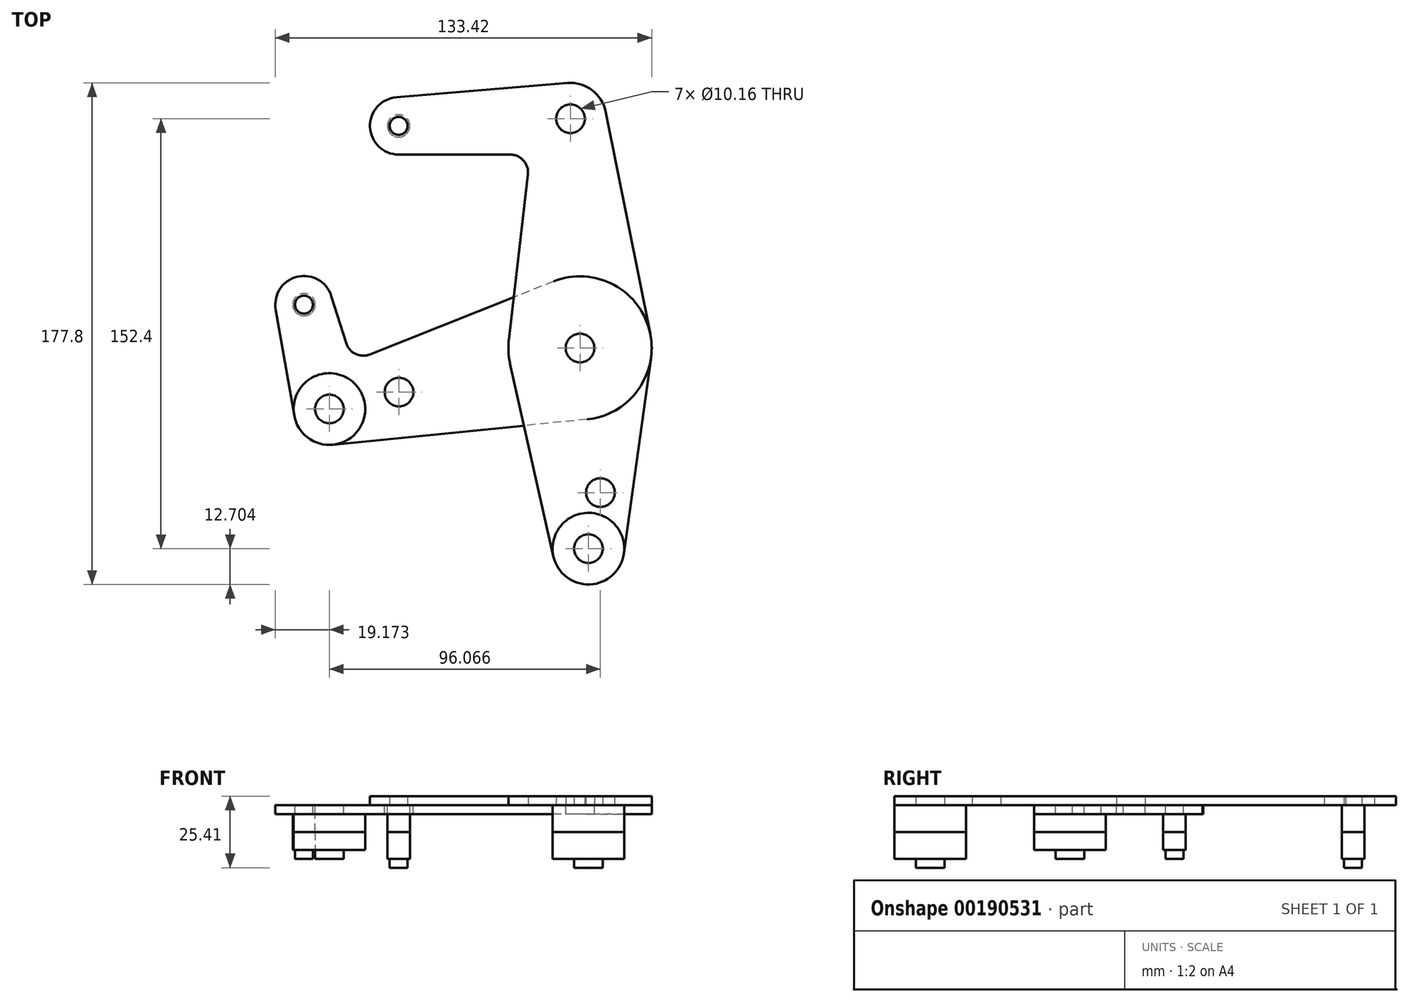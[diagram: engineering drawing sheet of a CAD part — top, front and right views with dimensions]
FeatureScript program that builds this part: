
annotation { "Feature Type Name" : "Feature", "Feature Type Description" : "" }
export const myFeature = defineFeature(function(context is Context, id is Id, definition is map)
    precondition{}
    {
        {
            var Q0;
            Q0=qCreatedBy(makeId("Top.planeOp"),FACE);
            var sketch = newSketch(context, id + "F0", { "sketchPlane" : qUnion([Q0])});
            skCircle(sketch, "E0", {"center": v(60.9, 102.91) * mm, "radius": 12.7 * mm});
            skCircle(sketch, "E1", {"center": v(60.9, 102.91) * mm, "radius": 5.08 * mm});
            skCircle(sketch, "E2", {"center": v(0, 100.37) * mm, "radius": 10.16 * mm});
            skCircle(sketch, "E3", {"center": v(0, 100.37) * mm, "radius": 3.18 * mm});
            skCircle(sketch, "E4", {"center": v(64.3, 21.63) * mm, "radius": 5.08 * mm});
            skCircle(sketch, "E5", {"center": v(64.3, 21.63) * mm, "radius": 25.4 * mm});
            skLineSegment(sketch, "E6", {"start": v(73.36, 105.42) * mm, "end": v(89.2, 26.64) * mm});
            skLineSegment(sketch, "E7", {"start": v(59.85, 115.57) * mm, "end": v(-0.85, 110.5) * mm});
            skCircle(sketch, "E8", {"center": v(-33.56, 37.02) * mm, "radius": 10.16 * mm});
            skCircle(sketch, "E9", {"center": v(-33.56, 37.02) * mm, "radius": 3.18 * mm});
            skCircle(sketch, "E10", {"center": v(-24.55, 0) * mm, "radius": 12.7 * mm});
            skCircle(sketch, "E11", {"center": v(-24.55, 0) * mm, "radius": 5.08 * mm});
            skCircle(sketch, "E12", {"center": v(67.26, -49.49) * mm, "radius": 12.7 * mm});
            skCircle(sketch, "E13", {"center": v(67.26, -49.49) * mm, "radius": 5.08 * mm});
            skLineSegment(sketch, "E14", {"start": v(60.9, 102.91) * mm, "end": v(0, 100.37) * mm, "construction": true});
            skLineSegment(sketch, "E15", {"start": v(89.46, 18.15) * mm, "end": v(79.84, -51.23) * mm});
            skLineSegment(sketch, "E16", {"start": v(39.51, 16.06) * mm, "end": v(54.87, -52.27) * mm});
            skLineSegment(sketch, "E17", {"start": v(-43.57, 35.28) * mm, "end": v(-37.06, -2.18) * mm});
            skLineSegment(sketch, "E18", {"start": v(66.82, -3.64) * mm, "end": v(-23.29, -12.64) * mm});
            skLineSegment(sketch, "E19", {"start": v(-33.56, 37.02) * mm, "end": v(-24.55, 0) * mm, "construction": true});
            skLineSegment(sketch, "E20", {"start": v(64.3, 21.63) * mm, "end": v(-24.55, 0) * mm, "construction": true});
            skCircle(sketch, "E21", {"center": v(71.52, -29.62) * mm, "radius": 5.08 * mm});
            skCircle(sketch, "E22", {"center": v(0.13, 6) * mm, "radius": 5.08 * mm});
            skLineSegment(sketch, "E23", {"start": v(39.06, 24.55) * mm, "end": v(45.84, 83.14) * mm});
            skLineSegment(sketch, "E24", {"start": v(0, 90.21) * mm, "end": v(39.53, 90.21) * mm});
            skLineSegment(sketch, "E25", {"start": v(-23.87, 40.07) * mm, "end": v(-18.6, 23.36) * mm});
            skLineSegment(sketch, "E26", {"start": v(54.92, 45.24) * mm, "end": v(-10.2, 19.37) * mm});
            skLineSegment(sketch, "E27", {"start": v(60.9, 102.91) * mm, "end": v(64.3, 21.63) * mm, "construction": true});
            skLineSegment(sketch, "E28", {"start": v(64.3, 21.63) * mm, "end": v(67.26, -49.49) * mm, "construction": true});
            skArc(sketch, "E29.filletArc", {"start": v(45.84, 83.14) * mm, "mid": v(44.27, 88.09) * mm, "end": v(39.53, 90.21) * mm});
            skArc(sketch, "E30.filletArc", {"start": v(-18.6, 23.36) * mm, "mid": v(-15.27, 19.53) * mm, "end": v(-10.2, 19.37) * mm});
            skSolve(sketch);
        }
        {
            var Q0;
            Q0=makeQuery(id+"F0.imprint","IMPRINT",FACE,{"disambiguationData":[TD([[makeQuery(id+"F0.imprint","IMPRINT",EDGE,{"derivedFrom":sQuery(id+"F0.wireOp",EDGE,"E1")}),-1.0]])]});
            var Q1;
            Q1=makeQuery(id+"F0.imprint","IMPRINT",FACE,{"disambiguationData":[TD([[makeQuery(id+"F0.imprint","IMPRINT",EDGE,{"derivedFrom":sQuery(id+"F0.wireOp",EDGE,"E3")}),-1.0]])]});
            var Q2;
            Q2=makeQuery(id+"F0.imprint","IMPRINT",FACE,{"disambiguationData":[TD([[makeQuery(id+"F0.imprint","IMPRINT",EDGE,{"derivedFrom":sQuery(id+"F0.wireOp",EDGE,"E13")}),-1.0]])]});
            var Q3;
            {var subQ0=sQuery(id+"F0.wireOp",EDGE,"E23");var subQ1=sQuery(id+"F0.wireOp",EDGE,"E5");var subQ2=makeQuery(id+"F0.imprint","INTERSECT",VERTEX,{"derivedFrom":[subQ1,subQ0]});Q3=makeQuery(id+"F0.imprint","IMPRINT",FACE,{"disambiguationData":[TD([[makeQuery(id+"F0.imprint","IMPRINT",EDGE,{"disambiguationData":[TD([[subQ2,1.0]])],"derivedFrom":subQ1}),-1.0]])]});}
            var Q4;
            {var subQ0=sQuery(id+"F0.wireOp",EDGE,"E16");var subQ1=sQuery(id+"F0.wireOp",EDGE,"E5");var subQ2=makeQuery(id+"F0.imprint","INTERSECT",VERTEX,{"derivedFrom":[subQ1,subQ0]});Q4=makeQuery(id+"F0.imprint","IMPRINT",FACE,{"disambiguationData":[TD([[makeQuery(id+"F0.imprint","IMPRINT",EDGE,{"disambiguationData":[TD([[subQ2,-1.0]])],"derivedFrom":subQ1}),-1.0]])]});}
            var Q5;
            {var subQ0=sQuery(id+"F0.wireOp",EDGE,"E6");Q5=makeQuery(id+"F0.imprint","IMPRINT",FACE,{"disambiguationData":[TD([[makeQuery(id+"F0.imprint","IMPRINT",EDGE,{"derivedFrom":subQ0}),-1.0]])]});}
            var Q6;
            {var subQ5=sQuery(id+"F0.wireOp",EDGE,"E15");Q6=makeQuery(id+"F0.imprint","IMPRINT",FACE,{"disambiguationData":[TD([[makeQuery(id+"F0.imprint","IMPRINT",EDGE,{"derivedFrom":subQ5}),-1.0]])]});}
            var Q7;
            Q7=makeQuery(id+"F0.imprint","IMPRINT",FACE,{"disambiguationData":[TD([[makeQuery(id+"F0.imprint","IMPRINT",EDGE,{"derivedFrom":sQuery(id+"F0.wireOp",EDGE,"E4")}),-1.0]])]});
            extrude(context, id + "F1", {"entities" : qUnion([Q0, Q1, Q2, Q3, Q4, Q5, Q6, Q7]), "depth" : 3.17 * mm});
        }
        {
            var Q0;
            {var subQ13=sQuery(id+"F0.wireOp",EDGE,"E17");Q0=makeQuery(id+"F0.imprint","IMPRINT",FACE,{"disambiguationData":[TD([[makeQuery(id+"F0.imprint","IMPRINT",EDGE,{"derivedFrom":subQ13}),1.0]])]});}
            var Q1;
            Q1=makeQuery(id+"F0.imprint","IMPRINT",FACE,{"disambiguationData":[TD([[makeQuery(id+"F0.imprint","IMPRINT",EDGE,{"derivedFrom":sQuery(id+"F0.wireOp",EDGE,"E11")}),-1.0]])]});
            var Q2;
            Q2=makeQuery(id+"F0.imprint","IMPRINT",FACE,{"disambiguationData":[TD([[makeQuery(id+"F0.imprint","IMPRINT",EDGE,{"derivedFrom":sQuery(id+"F0.wireOp",EDGE,"E9")}),-1.0]])]});
            var Q3;
            Q3=makeQuery(id+"F0.imprint","IMPRINT",FACE,{"disambiguationData":[TD([[makeQuery(id+"F0.imprint","IMPRINT",EDGE,{"derivedFrom":sQuery(id+"F0.wireOp",EDGE,"E4")}),-1.0]])]});
            var Q4;
            {var subQ0=sQuery(id+"F0.wireOp",EDGE,"E16");var subQ1=sQuery(id+"F0.wireOp",EDGE,"E5");var subQ2=makeQuery(id+"F0.imprint","INTERSECT",VERTEX,{"derivedFrom":[subQ1,subQ0]});Q4=makeQuery(id+"F0.imprint","IMPRINT",FACE,{"disambiguationData":[TD([[makeQuery(id+"F0.imprint","IMPRINT",EDGE,{"disambiguationData":[TD([[subQ2,-1.0]])],"derivedFrom":subQ1}),-1.0]])]});}
            var Q5;
            {var subQ0=sQuery(id+"F0.wireOp",EDGE,"E23");var subQ1=sQuery(id+"F0.wireOp",EDGE,"E5");var subQ2=makeQuery(id+"F0.imprint","INTERSECT",VERTEX,{"derivedFrom":[subQ1,subQ0]});Q5=makeQuery(id+"F0.imprint","IMPRINT",FACE,{"disambiguationData":[TD([[makeQuery(id+"F0.imprint","IMPRINT",EDGE,{"disambiguationData":[TD([[subQ2,1.0]])],"derivedFrom":subQ1}),-1.0]])]});}
            extrude(context, id + "F2", {"entities" : qUnion([Q0, Q1, Q2, Q3, Q4, Q5]), "oppositeDirection" : true, "depth" : 3.17 * mm});
        }
        {
            var Q0;
            Q0=makeQuery(id+"F1.opExtrude","CAP_FACE",FACE,{"disambiguationData":[OSD([sQuery(id+"F0.wireOp",EDGE,"E0"),sQuery(id+"F0.wireOp",EDGE,"E1"),sQuery(id+"F0.wireOp",EDGE,"E2"),sQuery(id+"F0.wireOp",EDGE,"E3"),sQuery(id+"F0.wireOp",EDGE,"E4"),sQuery(id+"F0.wireOp",EDGE,"E5"),sQuery(id+"F0.wireOp",EDGE,"E6"),sQuery(id+"F0.wireOp",EDGE,"E7"),sQuery(id+"F0.wireOp",EDGE,"E12"),sQuery(id+"F0.wireOp",EDGE,"E13"),sQuery(id+"F0.wireOp",EDGE,"E15"),sQuery(id+"F0.wireOp",EDGE,"E16"),sQuery(id+"F0.wireOp",EDGE,"E21"),sQuery(id+"F0.wireOp",EDGE,"E23"),sQuery(id+"F0.wireOp",EDGE,"E24"),sQuery(id+"F0.wireOp",EDGE,"E29.filletArc")])],"isStart":false});
            var sketch = newSketch(context, id + "F3", { "sketchPlane" : qUnion([Q0])});
            skCircle(sketch, "E31", {"center": v(67.26, -49.49) * mm, "radius": 12.7 * mm});
            skCircle(sketch, "E32", {"center": v(0, 100.37) * mm, "radius": 3.97 * mm});
            skSolve(sketch);
        }
        {
            var Q0;
            {var subQ13=sQuery(id+"F0.wireOp",EDGE,"E17");Q0=makeQuery(id+"F0.imprint","IMPRINT",FACE,{"disambiguationData":[TD([[makeQuery(id+"F0.imprint","IMPRINT",EDGE,{"derivedFrom":subQ13}),1.0]])]});}
            var sketch = newSketch(context, id + "F4", { "sketchPlane" : qUnion([Q0])});
            skCircle(sketch, "E33", {"center": v(-24.55, 0) * mm, "radius": 12.7 * mm});
            skCircle(sketch, "E34", {"center": v(-33.56, 37.02) * mm, "radius": 3.97 * mm});
            skSolve(sketch);
        }
        {
            var Q0;
            Q0=makeQuery(id+"F2.opExtrude","CAP_FACE",FACE,{"disambiguationData":[OSD([sQuery(id+"F0.wireOp",EDGE,"E4"),sQuery(id+"F0.wireOp",EDGE,"E5"),sQuery(id+"F0.wireOp",EDGE,"E8"),sQuery(id+"F0.wireOp",EDGE,"E9"),sQuery(id+"F0.wireOp",EDGE,"E10"),sQuery(id+"F0.wireOp",EDGE,"E11"),sQuery(id+"F0.wireOp",EDGE,"E17"),sQuery(id+"F0.wireOp",EDGE,"E18"),sQuery(id+"F0.wireOp",EDGE,"E22"),sQuery(id+"F0.wireOp",EDGE,"E25"),sQuery(id+"F0.wireOp",EDGE,"E26"),sQuery(id+"F0.wireOp",EDGE,"E30.filletArc")])],"isStart":false});
            cPlane(context, id + "F5", {"entities" : qUnion([Q0]), "cplaneType" : CPlaneType.OFFSET, "offset" : 6.35 * mm, "width" : 152.4 * mm, "height" : 152.4 * mm});
        }
        {
            var Q0;
            Q0 = qSketchRegion(id + "F3", true);
            var Q1;
            Q1 = qSketchRegion(id + "F4", true);
            var Q2;
            Q2=qCreatedBy(id+"F5.planeOp",FACE);
            extrude(context, id + "F6", {"entities" : qUnion([Q0, Q1]), "endBound" : BoundingType.UP_TO_SURFACE, "oppositeDirection" : true, "endBoundEntityFace" : qUnion([Q2]), "depth" : 25.4 * mm});
        }
        {
            var Q0;
            Q0=makeQuery(id+"F1.opExtrude","SWEPT_BODY",BODY,{"disambiguationData":[OSD([sQuery(id+"F0.wireOp",EDGE,"E0"),sQuery(id+"F0.wireOp",EDGE,"E1"),sQuery(id+"F0.wireOp",EDGE,"E2"),sQuery(id+"F0.wireOp",EDGE,"E3"),sQuery(id+"F0.wireOp",EDGE,"E4"),sQuery(id+"F0.wireOp",EDGE,"E5"),sQuery(id+"F0.wireOp",EDGE,"E6"),sQuery(id+"F0.wireOp",EDGE,"E7"),sQuery(id+"F0.wireOp",EDGE,"E12"),sQuery(id+"F0.wireOp",EDGE,"E13"),sQuery(id+"F0.wireOp",EDGE,"E15"),sQuery(id+"F0.wireOp",EDGE,"E16"),sQuery(id+"F0.wireOp",EDGE,"E21"),sQuery(id+"F0.wireOp",EDGE,"E23"),sQuery(id+"F0.wireOp",EDGE,"E24"),sQuery(id+"F0.wireOp",EDGE,"E29.filletArc")])]});
            var Q1;
            Q1=makeQuery(id+"F2.opExtrude","SWEPT_BODY",BODY,{"disambiguationData":[OSD([sQuery(id+"F0.wireOp",EDGE,"E4"),sQuery(id+"F0.wireOp",EDGE,"E5"),sQuery(id+"F0.wireOp",EDGE,"E8"),sQuery(id+"F0.wireOp",EDGE,"E9"),sQuery(id+"F0.wireOp",EDGE,"E10"),sQuery(id+"F0.wireOp",EDGE,"E11"),sQuery(id+"F0.wireOp",EDGE,"E17"),sQuery(id+"F0.wireOp",EDGE,"E18"),sQuery(id+"F0.wireOp",EDGE,"E22"),sQuery(id+"F0.wireOp",EDGE,"E25"),sQuery(id+"F0.wireOp",EDGE,"E26"),sQuery(id+"F0.wireOp",EDGE,"E30.filletArc")])]});
            var Q2;
            Q2=makeQuery(id+"F6.opExtrude","SWEPT_BODY",BODY,{"disambiguationData":[OSD([sQuery(id+"F4.wireOp",EDGE,"E33")])]});
            var Q3;
            Q3=makeQuery(id+"F6.opExtrude","SWEPT_BODY",BODY,{"disambiguationData":[OSD([sQuery(id+"F3.wireOp",EDGE,"E31")])]});
            var Q4;
            Q4=makeQuery(id+"F6.opExtrude","SWEPT_BODY",BODY,{"disambiguationData":[OSD([sQuery(id+"F3.wireOp",EDGE,"E32")])]});
            var Q5;
            Q5=makeQuery(id+"F6.opExtrude","SWEPT_BODY",BODY,{"disambiguationData":[OSD([sQuery(id+"F4.wireOp",EDGE,"E34")])]});
            booleanBodies(context, id + "F7", {"operationType" : BooleanOperationType.SUBTRACTION, "tools" : qUnion([Q0, Q1]), "targets" : qUnion([Q2, Q3, Q4, Q5]), "keepTools" : true});
        }
        {
            var Q0;
            Q0=makeQuery(id+"F6.opExtrude","SWEPT_BODY",BODY,{"disambiguationData":[OSD([sQuery(id+"F3.wireOp",EDGE,"E31")])]});
            var Q1;
            Q1=makeQuery(id+"F6.opExtrude","SWEPT_BODY",BODY,{"disambiguationData":[OSD([sQuery(id+"F3.wireOp",EDGE,"E32")])]});
            var Q2;
            Q2=makeQuery(id+"F6.opExtrude","SWEPT_BODY",BODY,{"disambiguationData":[OSD([sQuery(id+"F4.wireOp",EDGE,"E33")])]});
            var Q3;
            Q3=makeQuery(id+"F6.opExtrude","SWEPT_BODY",BODY,{"disambiguationData":[OSD([sQuery(id+"F4.wireOp",EDGE,"E34")])]});
            var Q4;
            Q4=qCreatedBy(id+"F5.planeOp",FACE);
            mirror(context, id + "F8", {"entities" : qUnion([Q0, Q1, Q2, Q3]), "mirrorPlane" : qUnion([Q4])});
        }
    });
